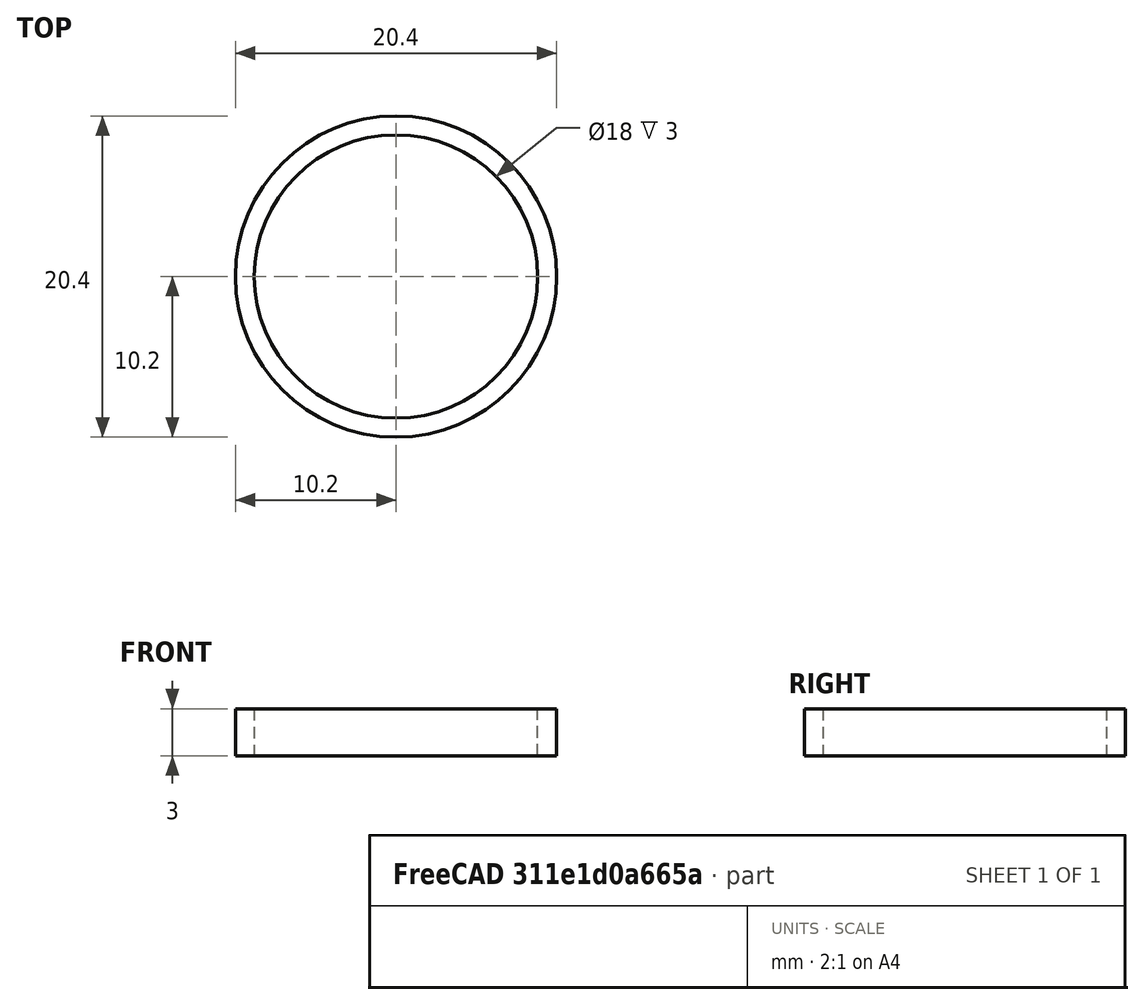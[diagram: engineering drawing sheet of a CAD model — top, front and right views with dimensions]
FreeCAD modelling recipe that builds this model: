
FCSTD DOCUMENT  (FreeCAD 0.21R33771 (Git))
Label: motor_thrust_ring
License: All rights reserved
LicenseURL: http://en.wikipedia.org/wiki/All_rights_reserved
objects: Sketcher::SketchObject×1, PartDesign::Pad×1, PartDesign::Body×1
note: 4 computed .brp shape members not serialized (recipe doc carries the construction recipe); baked Part::Feature solids carry a one-line shape summary decoded from their .brp

FEATURE [Sketcher::SketchObject] Sketch
  FullyConstrained = true
  MapMode = 5
  Support = -> [XY_Plane]
  sketch-geometry (2):
    g0: Circle CenterX=0 CenterY=0 CenterZ=0 NormalX=0 NormalY=0 NormalZ=1 AngleXU=0 Radius=9
    g1: Circle CenterX=0 CenterY=0 CenterZ=0 NormalX=0 NormalY=0 NormalZ=1 AngleXU=0 Radius=10.2
  constraints (4):
    c: Coincident(g0,g-1)
    c: Coincident(g1,g0)
    c: Radius(g1) = 10.2
    c: Radius(g0) = 9
FEATURE [PartDesign::Pad] Pad
  Direction = (0,0,1)
  Length = 3
  Length2 = 10
  Profile = -> Sketch
  ReferenceAxis = -> Sketch [N_Axis]
  Type = 0
FEATURE [PartDesign::Body] Body
  Group = -> [Sketch,Pad]
  Origin = -> Origin
  Tip = -> Pad
